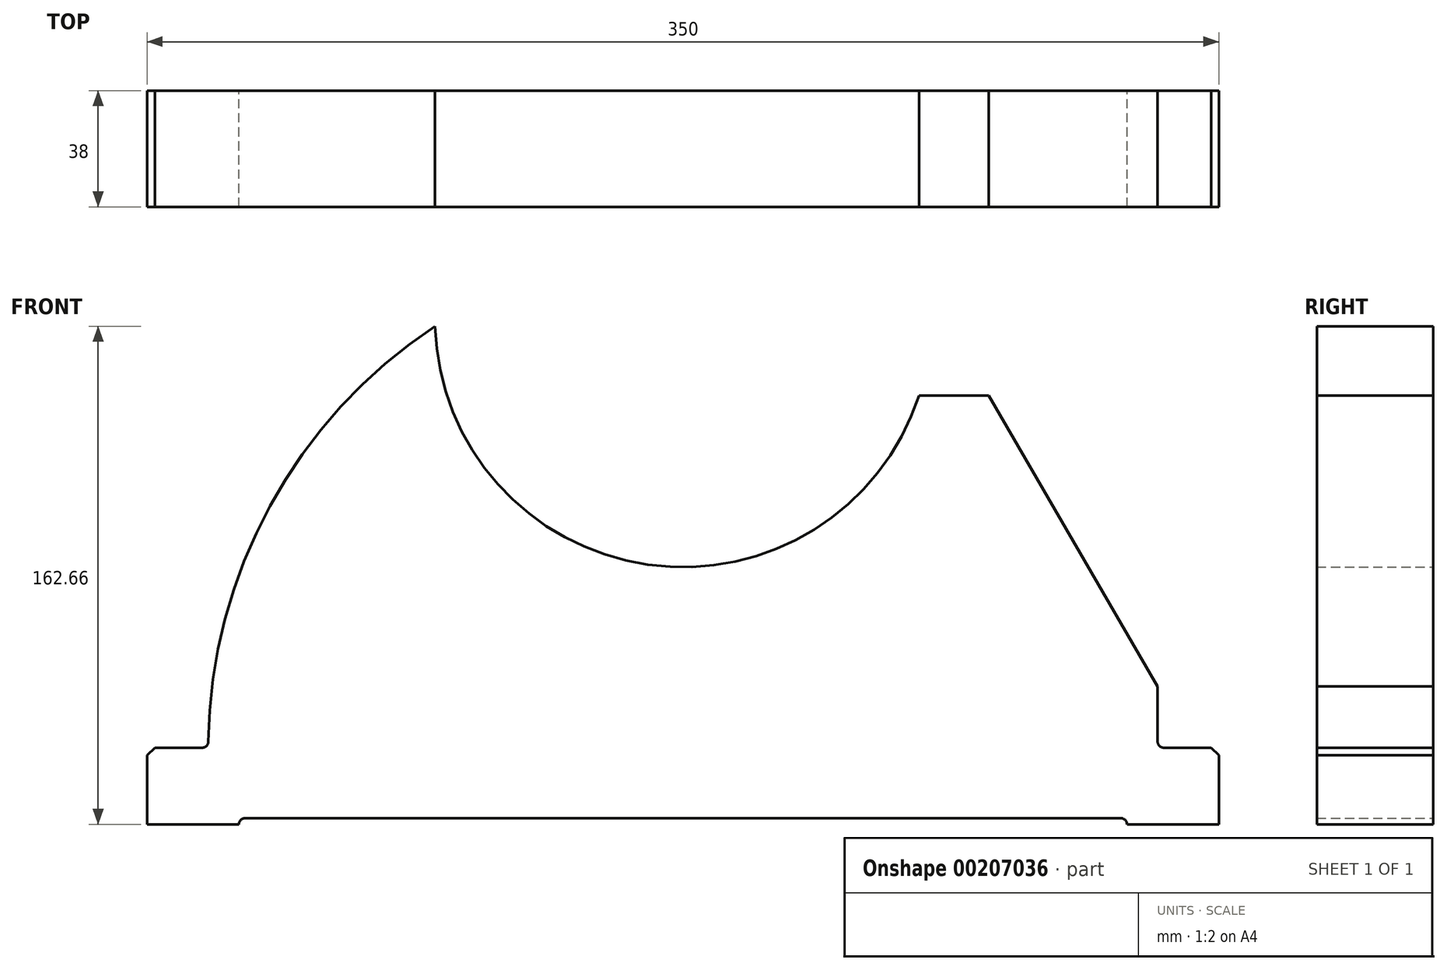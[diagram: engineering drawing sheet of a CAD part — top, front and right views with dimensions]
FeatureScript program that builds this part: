
annotation { "Feature Type Name" : "Feature", "Feature Type Description" : "" }
export const myFeature = defineFeature(function(context is Context, id is Id, definition is map)
    precondition{}
    {
        {
            var Q0;
            Q0=qCreatedBy(makeId("Front.planeOp"),FACE);
            var sketch = newSketch(context, id + "F0", { "sketchPlane" : qUnion([Q0])});
            skLineSegment(sketch, "E0", {"start": v(485, -202.35) * mm, "end": v(515, -202.35) * mm});
            skLineSegment(sketch, "E1", {"start": v(805, -202.35) * mm, "end": v(835, -202.35) * mm});
            skLineSegment(sketch, "E2", {"start": v(817, -177.35) * mm, "end": v(832.5, -177.35) * mm});
            skLineSegment(sketch, "E3", {"start": v(485, -179.85) * mm, "end": v(485, -202.35) * mm});
            skLineSegment(sketch, "E4", {"start": v(835, -179.85) * mm, "end": v(835, -202.35) * mm});
            skLineSegment(sketch, "E5", {"start": v(515, -200.35) * mm, "end": v(803, -200.35) * mm});
            skArc(sketch, "E6", {"start": v(579.04, -39.7) * mm, "mid": v(648.5, -117.53) * mm, "end": v(737.05, -62.35) * mm});
            skLineSegment(sketch, "E7", {"start": v(815, -157.35) * mm, "end": v(759.84, -62.35) * mm});
            skArc(sketch, "E8", {"start": v(579.04, -39.7) * mm, "mid": v(525.16, -98.33) * mm, "end": v(505.02, -175.38) * mm});
            skLineSegment(sketch, "E9", {"start": v(737.05, -62.35) * mm, "end": v(759.84, -62.35) * mm});
            skArc(sketch, "E10", {"start": v(517, -200.35) * mm, "mid": v(515.6, -200.94) * mm, "end": v(515, -202.35) * mm});
            skArc(sketch, "E11", {"start": v(805, -202.35) * mm, "mid": v(804.42, -200.94) * mm, "end": v(803, -200.35) * mm});
            skLineSegment(sketch, "E12", {"start": v(485, -179.85) * mm, "end": v(487.5, -177.35) * mm});
            skLineSegment(sketch, "E13", {"start": v(832.5, -177.35) * mm, "end": v(835, -179.85) * mm});
            skLineSegment(sketch, "E14", {"start": v(487.5, -177.35) * mm, "end": v(503.02, -177.35) * mm});
            skArc(sketch, "E15", {"start": v(503.02, -177.35) * mm, "mid": v(504.42, -176.78) * mm, "end": v(505.02, -175.38) * mm});
            skLineSegment(sketch, "E16", {"start": v(815, -157.35) * mm, "end": v(815, -175.35) * mm});
            skArc(sketch, "E17", {"start": v(815, -175.35) * mm, "mid": v(815.6, -176.77) * mm, "end": v(817, -177.35) * mm});
            skSolve(sketch);
        }
        {
            var Q0;
            Q0=makeQuery(id+"F0.imprint","IMPRINT",FACE,{"disambiguationData":[TD([[makeQuery(id+"F0.imprint","IMPRINT",EDGE,{"derivedFrom":sQuery(id+"F0.wireOp",EDGE,"E0")}),1.0]])]});
            extrude(context, id + "F1", {"entities" : qUnion([Q0]), "depth" : 38 * mm});
        }
    });
